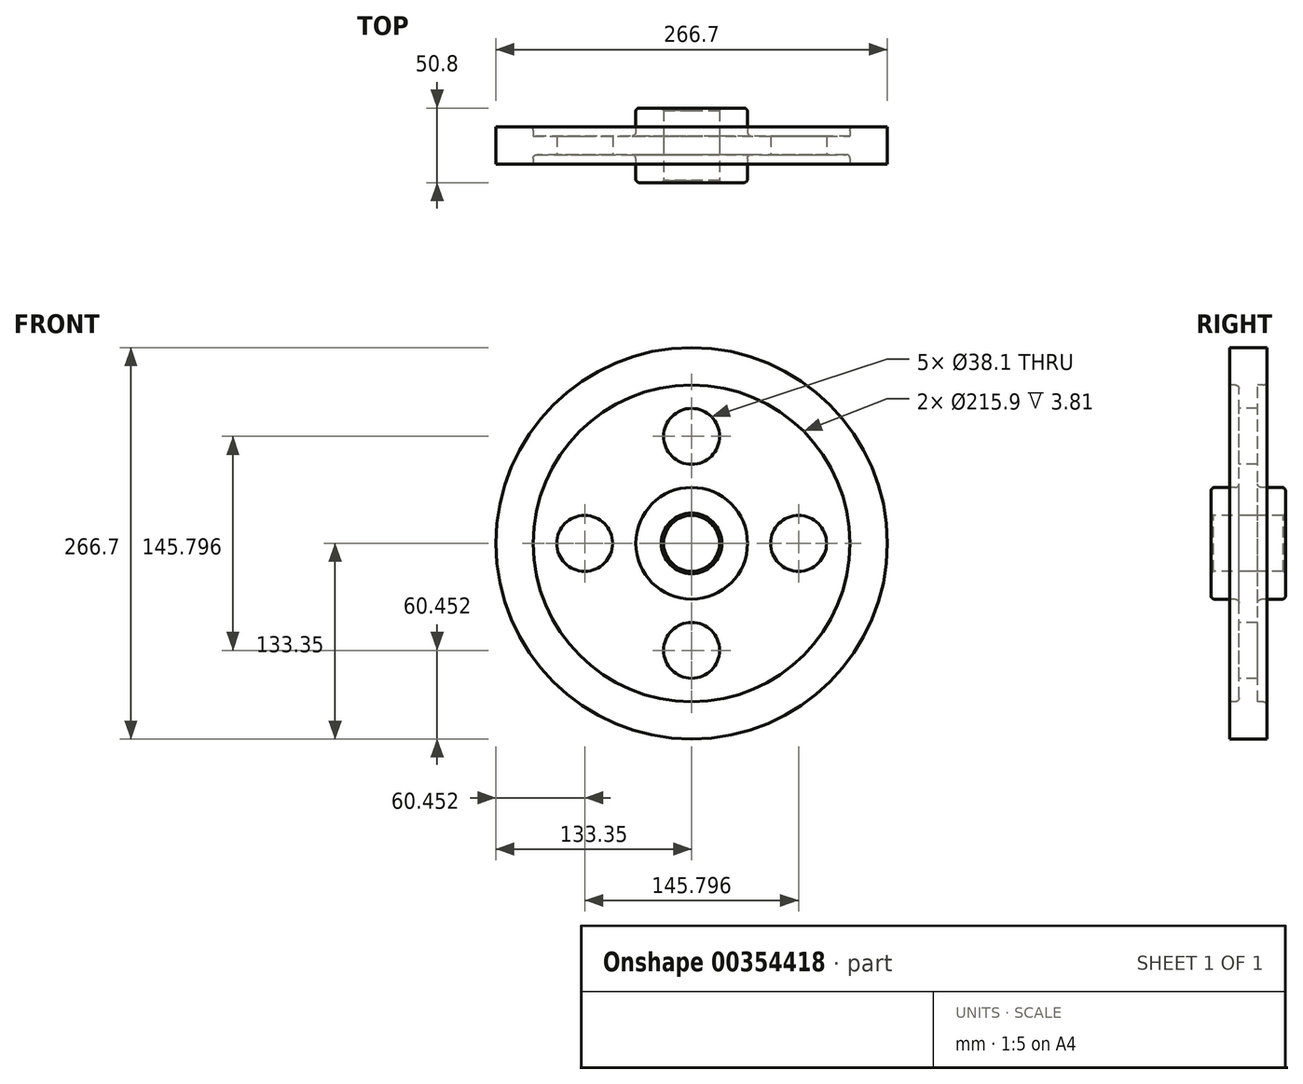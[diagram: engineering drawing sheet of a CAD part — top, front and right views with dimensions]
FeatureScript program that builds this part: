
annotation { "Feature Type Name" : "Feature", "Feature Type Description" : "" }
export const myFeature = defineFeature(function(context is Context, id is Id, definition is map)
    precondition{}
    {
        {
            var Q0;
            Q0=qCreatedBy(makeId("Right.planeOp"),FACE);
            var sketch = newSketch(context, id + "F0", { "sketchPlane" : qUnion([Q0])});
            skLineSegment(sketch, "E0", {"start": v(0, 0) * mm, "end": v(0, 28.58) * mm});
            skLineSegment(sketch, "E1", {"start": v(0, 28.58) * mm, "end": v(0, 73.03) * mm});
            skLineSegment(sketch, "E2", {"start": v(0, 73.03) * mm, "end": v(0, 120.65) * mm});
            skLineSegment(sketch, "E3.bottom", {"start": v(25.4, 19.05) * mm, "end": v(-25.4, 19.05) * mm});
            skLineSegment(sketch, "E3.top", {"start": v(25.4, 38.1) * mm, "end": v(-25.4, 38.1) * mm});
            skLineSegment(sketch, "E3.left", {"start": v(25.4, 19.05) * mm, "end": v(25.4, 38.1) * mm});
            skLineSegment(sketch, "E3.right", {"start": v(-25.4, 19.05) * mm, "end": v(-25.4, 38.1) * mm});
            skPoint(sketch, "E3.middle", {"position": v(0, 28.58) * mm});
            skLineSegment(sketch, "E4.bottom", {"start": v(-12.7, 107.95) * mm, "end": v(12.7, 107.95) * mm});
            skLineSegment(sketch, "E4.top", {"start": v(-12.7, 133.35) * mm, "end": v(12.7, 133.35) * mm});
            skLineSegment(sketch, "E4.left", {"start": v(-12.7, 107.95) * mm, "end": v(-12.7, 133.35) * mm});
            skLineSegment(sketch, "E4.right", {"start": v(12.7, 107.95) * mm, "end": v(12.7, 133.35) * mm});
            skPoint(sketch, "E4.middle", {"position": v(0, 120.65) * mm});
            skLineSegment(sketch, "E5.left", {"start": v(-6.35, 34.93) * mm, "end": v(-6.35, 111.12) * mm});
            skLineSegment(sketch, "E5.right", {"start": v(6.35, 34.93) * mm, "end": v(6.35, 111.12) * mm});
            skPoint(sketch, "E5.middle", {"position": v(0, 73.03) * mm});
            skLineSegment(sketch, "E6", {"start": v(0, 28.58) * mm, "end": v(67.46, 28.58) * mm});
            skLineSegment(sketch, "E7", {"start": v(0, 0) * mm, "end": v(58.06, 0) * mm});
            skSolve(sketch);
        }
        {
            var Q0;
            Q0 = qSketchRegion(id + "F0", true);
            var Q1;
            Q1=sQuery(id+"F0.wireOp",EDGE,"E7");
            revolve(context, id + "F1", {"entities" : qUnion([Q0]), "axis" : qUnion([Q1]), "revolveType" : RevolveType.FULL});
        }
        {
            var Q0;
            Q0=makeQuery(id+"F1.opRevolve","SWEPT_FACE",FACE,{"disambiguationData":[OSD([sQuery(id+"F0.wireOp",EDGE,"E5.left")])]});
            var sketch = newSketch(context, id + "F2", { "sketchPlane" : qUnion([Q0])});
            skLineSegment(sketch, "E8", {"start": v(0, 0) * mm, "end": v(0, 72.9) * mm});
            skCircle(sketch, "E9", {"center": v(0, 72.9) * mm, "radius": 19.05 * mm});
            skCircle(sketch, "E10.1.0", {"center": v(-72.9, 0) * mm, "radius": 19.05 * mm});
            skCircle(sketch, "E10.2.0", {"center": v(0, -72.9) * mm, "radius": 19.05 * mm});
            skCircle(sketch, "E10.3.0", {"center": v(72.9, 0) * mm, "radius": 19.05 * mm});
            skPoint(sketch, "E10.center", {"position": v(0, 0) * mm});
            skSolve(sketch);
        }
        {
            var Q0;
            Q0=makeQuery(id+"F2.imprint","IMPRINT",FACE,{"disambiguationData":[TD([[makeQuery(id+"F2.imprint","IMPRINT",EDGE,{"derivedFrom":sQuery(id+"F2.wireOp",EDGE,"E9")}),1.0]])]});
            var Q1;
            Q1=makeQuery(id+"F2.imprint","IMPRINT",FACE,{"disambiguationData":[TD([[makeQuery(id+"F2.imprint","IMPRINT",EDGE,{"derivedFrom":sQuery(id+"F2.wireOp",EDGE,"E10.3.0")}),1.0]])]});
            var Q2;
            Q2=makeQuery(id+"F2.imprint","IMPRINT",FACE,{"disambiguationData":[TD([[makeQuery(id+"F2.imprint","IMPRINT",EDGE,{"derivedFrom":sQuery(id+"F2.wireOp",EDGE,"E10.2.0")}),1.0]])]});
            var Q3;
            Q3=makeQuery(id+"F2.imprint","IMPRINT",FACE,{"disambiguationData":[TD([[makeQuery(id+"F2.imprint","IMPRINT",EDGE,{"derivedFrom":sQuery(id+"F2.wireOp",EDGE,"E10.1.0")}),1.0]])]});
            extrude(context, id + "F3", {"entities" : qUnion([Q0, Q1, Q2, Q3]), "operationType" : NewBodyOperationType.REMOVE, "oppositeDirection" : true, "depth" : 25.4 * mm});
        }
        {
            var Q0;
            {var subQ0=sQuery(id+"F0.wireOp",EDGE,"E3.top");Q0=makeQuery(id+"F1.opRevolve","SWEPT_FACE",FACE,{"disambiguationData":[OSD([subQ0]),TDD([makeQuery(id+"F0.imprint","IMPRINT",EDGE,{"disambiguationData":[TD([[makeQuery(id+"F0.imprint","INTERSECT",VERTEX,{"derivedFrom":[subQ0,sQuery(id+"F0.wireOp",EDGE,"E3.right")]}),1.0]])],"derivedFrom":subQ0})])]});}
            var Q1;
            Q1=makeQuery(id+"F1.opRevolve","SWEPT_EDGE",EDGE,{"disambiguationData":[OSD([sQuery(id+"F0.wireOp",EDGE,"E4.bottom"),sQuery(id+"F0.wireOp",EDGE,"E5.left")])]});
            var Q2;
            {var subQ0=sQuery(id+"F0.wireOp",EDGE,"E3.top");Q2=makeQuery(id+"F1.opRevolve","SWEPT_FACE",FACE,{"disambiguationData":[OSD([subQ0]),TDD([makeQuery(id+"F0.imprint","IMPRINT",EDGE,{"disambiguationData":[TD([[makeQuery(id+"F0.imprint","INTERSECT",VERTEX,{"derivedFrom":[subQ0,sQuery(id+"F0.wireOp",EDGE,"E3.left")]}),-1.0]])],"derivedFrom":subQ0})])]});}
            var Q3;
            Q3=makeQuery(id+"F1.opRevolve","SWEPT_EDGE",EDGE,{"disambiguationData":[OSD([sQuery(id+"F0.wireOp",EDGE,"E4.bottom"),sQuery(id+"F0.wireOp",EDGE,"E4.right")])]});
            fillet(context, id + "F4", {"entities" : qUnion([Q0, Q1, Q2, Q3]), "radius" : 2.54 * mm, "tangentPropagation" : true, "allowEdgeOverflow" : false});
        }
        {
            var Q0;
            Q0=makeQuery(id+"F1.opRevolve","SWEPT_EDGE",EDGE,{"disambiguationData":[OSD([sQuery(id+"F0.wireOp",EDGE,"E3.bottom"),sQuery(id+"F0.wireOp",EDGE,"E3.left")])]});
            var Q1;
            Q1=makeQuery(id+"F1.opRevolve","SWEPT_EDGE",EDGE,{"disambiguationData":[OSD([sQuery(id+"F0.wireOp",EDGE,"E3.bottom"),sQuery(id+"F0.wireOp",EDGE,"E3.right")])]});
            chamfer(context, id + "F5", {"entities" : qUnion([Q0, Q1]), "width" : 1.59 * mm, "tangentPropagation" : true});
        }
    });
